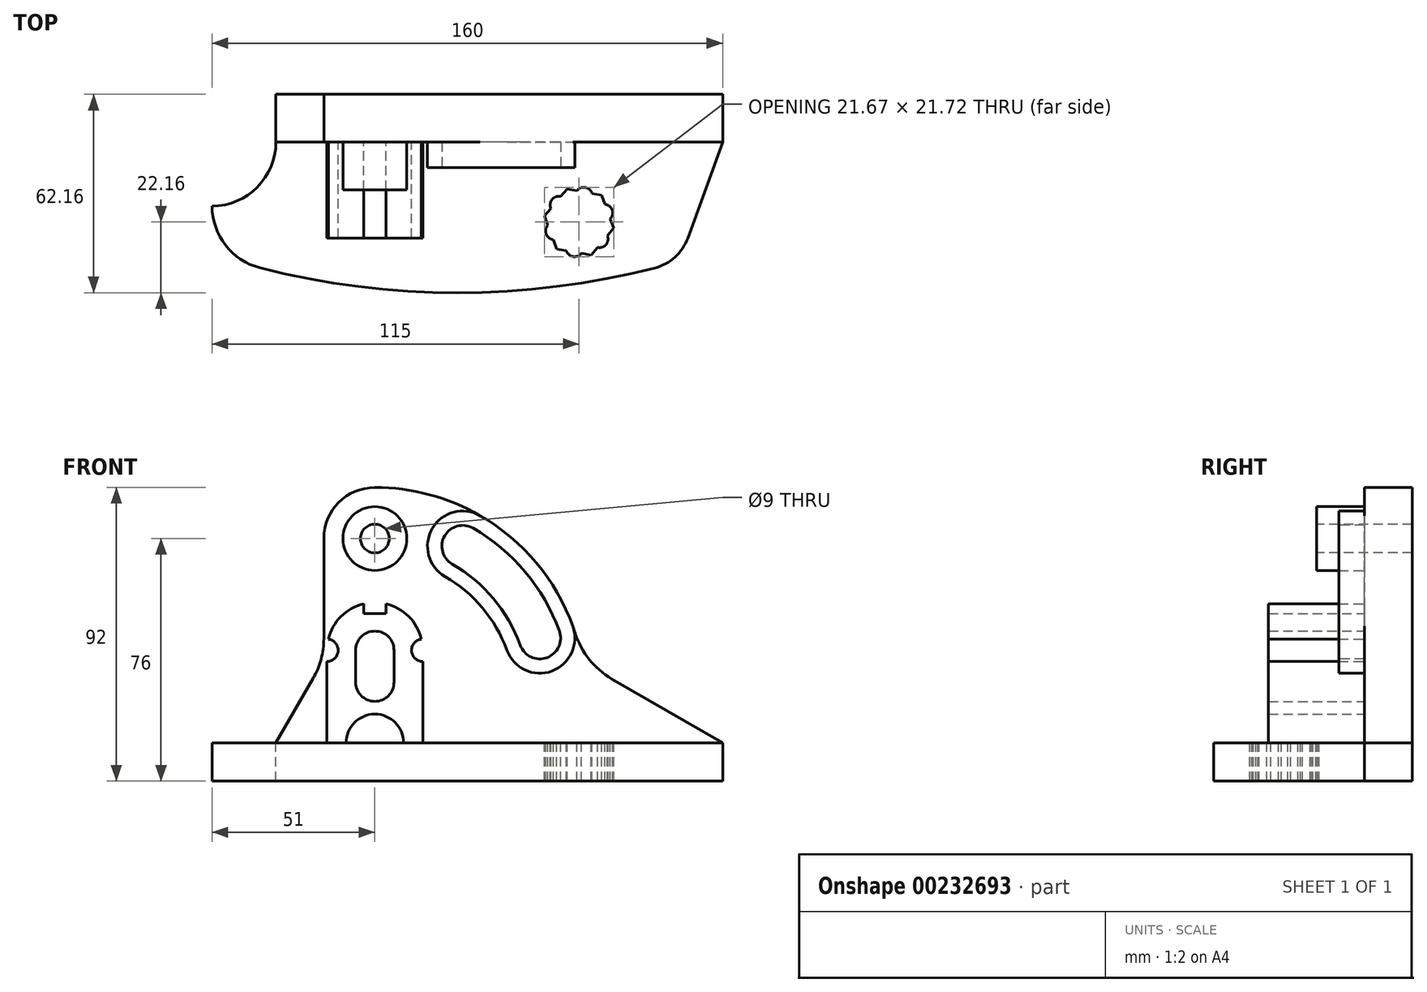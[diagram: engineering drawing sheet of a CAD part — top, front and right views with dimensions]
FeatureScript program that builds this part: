
annotation { "Feature Type Name" : "Feature", "Feature Type Description" : "" }
export const myFeature = defineFeature(function(context is Context, id is Id, definition is map)
    precondition{}
    {
        {
            var Q0;
            Q0=qCreatedBy(makeId("Top.planeOp"),FACE);
            var sketch = newSketch(context, id + "F0", { "sketchPlane" : qUnion([Q0])});
            skLineSegment(sketch, "E0", {"start": v(-31, 15) * mm, "end": v(-31, 0) * mm});
            skLineSegment(sketch, "E1", {"start": v(109, 15) * mm, "end": v(109, 0) * mm});
            skLineSegment(sketch, "E2", {"start": v(-31, 15) * mm, "end": v(109, 15) * mm});
            skLineSegment(sketch, "E3", {"start": v(109, 0) * mm, "end": v(98.08, -30) * mm});
            skArc(sketch, "E4", {"start": v(-51, -20) * mm, "mid": v(-36.86, -14.14) * mm, "end": v(-31, 0) * mm});
            skArc(sketch, "E5", {"start": v(-51, -20) * mm, "mid": v(-46.8, -32.27) * mm, "end": v(-35.95, -39.38) * mm});
            skLineSegment(sketch, "E6.0", {"start": v(94.9, 5.13) * mm, "end": v(83.99, -24.87) * mm, "construction": true});
            skArc(sketch, "E7", {"start": v(87.7, -39.4) * mm, "mid": v(94.05, -36) * mm, "end": v(98.08, -30) * mm});
            skLineSegment(sketch, "E8", {"start": v(98.08, -30) * mm, "end": v(83.99, -24.87) * mm, "construction": true});
            skArc(sketch, "E9", {"start": v(-35.95, -39.38) * mm, "mid": v(25.87, -47.16) * mm, "end": v(87.7, -39.4) * mm});
            skSolve(sketch);
        }
        {
            var Q0;
            Q0 = qSketchRegion(id + "F0", true);
            extrude(context, id + "F1", {"entities" : qUnion([Q0]), "oppositeDirection" : true, "depth" : 12 * mm});
        }
        {
            var Q0;
            Q0=qCreatedBy(makeId("Front.planeOp"),FACE);
            var sketch = newSketch(context, id + "F2", { "sketchPlane" : qUnion([Q0])});
            skLineSegment(sketch, "E10", {"start": v(109, 0) * mm, "end": v(74.16, 20.11) * mm});
            skLineSegment(sketch, "E11", {"start": v(-31, 0) * mm, "end": v(-19.35, 20.18) * mm});
            skLineSegment(sketch, "E12", {"start": v(-16, 65) * mm, "end": v(-16, 32.68) * mm});
            skArc(sketch, "E13.filletArc", {"start": v(-19.35, 20.18) * mm, "mid": v(-16.85, 26.2) * mm, "end": v(-16, 32.68) * mm});
            skArc(sketch, "E14", {"start": v(62.85, 34.14) * mm, "mid": v(38.9, 67.32) * mm, "end": v(0, 80) * mm});
            skArc(sketch, "E15", {"start": v(0, 80) * mm, "mid": v(-11.31, 75.31) * mm, "end": v(-16, 64) * mm});
            skArc(sketch, "E16", {"start": v(62.85, 34.14) * mm, "mid": v(67.2, 26.07) * mm, "end": v(74.16, 20.11) * mm});
            skLineSegment(sketch, "E17", {"start": v(-31, 0) * mm, "end": v(109, 0) * mm});
            skSolve(sketch);
        }
        {
            var Q0;
            Q0 = qSketchRegion(id + "F2", true);
            extrude(context, id + "F3", {"entities" : qUnion([Q0]), "operationType" : NewBodyOperationType.ADD, "oppositeDirection" : true, "depth" : 15 * mm});
        }
        {
            var Q0;
            Q0=makeQuery(id+"F3.opExtrude","CAP_FACE",FACE,{"disambiguationData":[OSD([sQuery(id+"F2.wireOp",EDGE,"E10"),sQuery(id+"F2.wireOp",EDGE,"E11"),sQuery(id+"F2.wireOp",EDGE,"E12"),sQuery(id+"F2.wireOp",EDGE,"E13.filletArc"),sQuery(id+"F2.wireOp",EDGE,"E14"),sQuery(id+"F2.wireOp",EDGE,"E15"),sQuery(id+"F2.wireOp",EDGE,"E16"),sQuery(id+"F2.wireOp",EDGE,"E17")])],"isStart":true});
            var sketch = newSketch(context, id + "F4", { "sketchPlane" : qUnion([Q0])});
            skLineSegment(sketch, "E18", {"start": v(15, 25.5) * mm, "end": v(15, 0) * mm});
            skLineSegment(sketch, "E19.MirrorCS", {"start": v(-15, 25.5) * mm, "end": v(-15, 0) * mm});
            skArc(sketch, "E20", {"start": v(14.6, 32.48) * mm, "mid": v(10.62, 39.6) * mm, "end": v(3.5, 43.59) * mm});
            skPoint(sketch, "E21.orphan", {"position": v(15, 56.83) * mm});
            skPoint(sketch, "E22.orphan", {"position": v(-15, 56.83) * mm});
            skLineSegment(sketch, "E23", {"start": v(-15, 0) * mm, "end": v(-9, 0) * mm});
            skPoint(sketch, "E24.orphan", {"position": v(-15, -26.65) * mm});
            skPoint(sketch, "E25.orphan", {"position": v(15, -26.65) * mm});
            skLineSegment(sketch, "E26", {"start": v(6, 29) * mm, "end": v(6, 19) * mm});
            skLineSegment(sketch, "E27.MirrorCS", {"start": v(-6, 29) * mm, "end": v(-6, 19) * mm});
            skArc(sketch, "E28", {"start": v(-6, 19) * mm, "mid": v(0, 13) * mm, "end": v(6, 19) * mm});
            skArc(sketch, "E29.trimOffspring", {"start": v(6, 29) * mm, "mid": v(0, 35) * mm, "end": v(-6, 29) * mm});
            skPoint(sketch, "E30.orphan", {"position": v(-6, 36.37) * mm});
            skPoint(sketch, "E31.orphan", {"position": v(6, 36.37) * mm});
            skPoint(sketch, "E32.orphan", {"position": v(-6, 6) * mm});
            skPoint(sketch, "E33.orphan", {"position": v(6, 6) * mm});
            skArc(sketch, "E34", {"start": v(9, 0) * mm, "mid": v(0, 9) * mm, "end": v(-9, 0) * mm});
            skLineSegment(sketch, "E35.trimOffspring", {"start": v(9, 0) * mm, "end": v(15, 0) * mm});
            skArc(sketch, "E36", {"start": v(14.6, 32.48) * mm, "mid": v(11.5, 28.8) * mm, "end": v(15, 25.5) * mm});
            skArc(sketch, "E37.MirrorC", {"start": v(-14.6, 32.48) * mm, "mid": v(-11.5, 28.8) * mm, "end": v(-15, 25.5) * mm});
            skLineSegment(sketch, "E38", {"start": v(3.5, 43.59) * mm, "end": v(3.5, 40.5) * mm});
            skLineSegment(sketch, "E39.MirrorCS", {"start": v(-3.5, 43.59) * mm, "end": v(-3.5, 40.5) * mm});
            skLineSegment(sketch, "E40", {"start": v(-3.5, 40.5) * mm, "end": v(3.5, 40.5) * mm});
            skArc(sketch, "E41.trimOffspring", {"start": v(-3.5, 43.59) * mm, "mid": v(-10.62, 39.6) * mm, "end": v(-14.6, 32.48) * mm});
            skPoint(sketch, "E42.orphan", {"position": v(-3.5, 47.7) * mm});
            skPoint(sketch, "E43.orphan", {"position": v(3.5, 47.7) * mm});
            skSolve(sketch);
        }
        {
            var Q0;
            Q0 = qSketchRegion(id + "F4", true);
            extrude(context, id + "F5", {"entities" : qUnion([Q0]), "operationType" : NewBodyOperationType.ADD, "depth" : 30 * mm});
        }
        {
            var Q0;
            {var subQ0=sQuery(id+"F2.wireOp",EDGE,"E12");var subQ1=sQuery(id+"F2.wireOp",EDGE,"E11");var subQ3=sQuery(id+"F2.wireOp",EDGE,"E14");var subQ6=sQuery(id+"F0.wireOp",EDGE,"E0");var subQ7=sQuery(id+"F2.wireOp",EDGE,"E10");var subQ8=sQuery(id+"F2.wireOp",EDGE,"E15");var subQ9=sQuery(id+"F2.wireOp",EDGE,"E13.filletArc");var subQ10=sQuery(id+"F2.wireOp",EDGE,"E16");Q0=makeQuery(id+"F5.boolean.opBoolean","SPLIT",FACE,{"disambiguationData":[TD([makeQuery(id+"F1.opExtrude","SWEPT_FACE",FACE,{"disambiguationData":[OSD([subQ6])]})])],"derivedFrom":makeQuery(id+"F3.opExtrude","CAP_FACE",FACE,{"disambiguationData":[OSD([subQ7,subQ1,subQ0,subQ9,subQ3,subQ8,subQ10,sQuery(id+"F2.wireOp",EDGE,"E17")])],"isStart":true})});}
            var sketch = newSketch(context, id + "F6", { "sketchPlane" : qUnion([Q0])});
            skCircle(sketch, "E44", {"center": v(0, 14) * mm, "radius": 55 * mm, "construction": true});
            skArc(sketch, "E45.0", {"start": v(57.8, 35.03) * mm, "mid": v(47.11, 53.53) * mm, "end": v(30.75, 67.26) * mm, "construction": true});
            skArc(sketch, "E46.0", {"start": v(45.58, 30.59) * mm, "mid": v(37.15, 45.18) * mm, "end": v(24.25, 56) * mm, "construction": true});
            skLineSegment(sketch, "E47", {"start": v(0, 14) * mm, "end": v(66.08, 38.05) * mm, "construction": true});
            skLineSegment(sketch, "E48", {"start": v(0, 14) * mm, "end": v(40.9, 84.85) * mm, "construction": true});
            skArc(sketch, "E49", {"start": v(30.75, 67.26) * mm, "mid": v(21.87, 64.88) * mm, "end": v(24.25, 56) * mm, "construction": true});
            skArc(sketch, "E50", {"start": v(45.58, 30.59) * mm, "mid": v(53.9, 26.7) * mm, "end": v(57.8, 35.03) * mm, "construction": true});
            skArc(sketch, "E51.0", {"start": v(41.35, 29.05) * mm, "mid": v(33.7, 42.28) * mm, "end": v(22, 52.1) * mm});
            skArc(sketch, "E52", {"start": v(33, 71.16) * mm, "mid": v(17.97, 67.13) * mm, "end": v(22, 52.1) * mm});
            skArc(sketch, "E53", {"start": v(41.35, 29.05) * mm, "mid": v(55.45, 22.47) * mm, "end": v(62.02, 36.57) * mm});
            skArc(sketch, "E54", {"start": v(62.02, 36.57) * mm, "mid": v(50.56, 56.42) * mm, "end": v(33, 71.16) * mm});
            skSolve(sketch);
        }
        {
            var Q0;
            Q0 = qSketchRegion(id + "F6", true);
            extrude(context, id + "F7", {"entities" : qUnion([Q0]), "operationType" : NewBodyOperationType.ADD, "depth" : 8 * mm});
        }
        {
            var Q0;
            Q0=makeQuery(id+"F7.opExtrude","CAP_FACE",FACE,{"disambiguationData":[OSD([sQuery(id+"F6.wireOp",EDGE,"E51.0"),sQuery(id+"F6.wireOp",EDGE,"E52"),sQuery(id+"F6.wireOp",EDGE,"E53"),sQuery(id+"F6.wireOp",EDGE,"E54")])],"isStart":false});
            var sketch = newSketch(context, id + "F8", { "sketchPlane" : qUnion([Q0])});
            skArc(sketch, "E55", {"start": v(27.5, 61.63) * mm, "mid": v(42.13, 49.35) * mm, "end": v(51.68, 32.81) * mm, "construction": true});
            skLineSegment(sketch, "E56", {"start": v(0, 14) * mm, "end": v(67.84, 38.7) * mm, "construction": true});
            skArc(sketch, "E57", {"start": v(30.75, 67.26) * mm, "mid": v(21.87, 64.88) * mm, "end": v(24.25, 56) * mm});
            skArc(sketch, "E58", {"start": v(45.58, 30.59) * mm, "mid": v(53.9, 26.7) * mm, "end": v(57.8, 35.03) * mm});
            skArc(sketch, "E59", {"start": v(24.25, 56) * mm, "mid": v(37.15, 45.18) * mm, "end": v(45.58, 30.59) * mm});
            skArc(sketch, "E60", {"start": v(30.75, 67.26) * mm, "mid": v(47.11, 53.53) * mm, "end": v(57.8, 35.03) * mm});
            skSolve(sketch);
        }
        {
            var Q0;
            Q0 = qSketchRegion(id + "F8", true);
            extrude(context, id + "F9", {"entities" : qUnion([Q0]), "operationType" : NewBodyOperationType.REMOVE, "oppositeDirection" : true, "depth" : 8 * mm});
        }
        {
            var Q0;
            {var subQ0=sQuery(id+"F2.wireOp",EDGE,"E12");var subQ1=sQuery(id+"F2.wireOp",EDGE,"E11");var subQ3=sQuery(id+"F2.wireOp",EDGE,"E14");var subQ6=sQuery(id+"F0.wireOp",EDGE,"E0");var subQ7=sQuery(id+"F2.wireOp",EDGE,"E10");var subQ8=sQuery(id+"F2.wireOp",EDGE,"E15");var subQ9=sQuery(id+"F2.wireOp",EDGE,"E13.filletArc");var subQ10=sQuery(id+"F2.wireOp",EDGE,"E16");Q0=makeQuery(id+"F5.boolean.opBoolean","SPLIT",FACE,{"disambiguationData":[TD([makeQuery(id+"F1.opExtrude","SWEPT_FACE",FACE,{"disambiguationData":[OSD([subQ6])]})])],"derivedFrom":makeQuery(id+"F3.opExtrude","CAP_FACE",FACE,{"disambiguationData":[OSD([subQ7,subQ1,subQ0,subQ9,subQ3,subQ8,subQ10,sQuery(id+"F2.wireOp",EDGE,"E17")])],"isStart":true})});}
            var sketch = newSketch(context, id + "F10", { "sketchPlane" : qUnion([Q0])});
            skCircle(sketch, "E61", {"center": v(0, 64) * mm, "radius": 10 * mm});
            skSolve(sketch);
        }
        {
            var Q0;
            Q0 = qSketchRegion(id + "F10", true);
            extrude(context, id + "F11", {"entities" : qUnion([Q0]), "operationType" : NewBodyOperationType.ADD, "depth" : 15 * mm});
        }
        {
            var Q0;
            Q0=makeQuery(id+"F11.opExtrude","CAP_FACE",FACE,{"disambiguationData":[OSD([sQuery(id+"F10.wireOp",EDGE,"E61")])],"isStart":false});
            var sketch = newSketch(context, id + "F12", { "sketchPlane" : qUnion([Q0])});
            skPoint(sketch, "E62", {"position": v(0, 64) * mm});
            skSolve(sketch);
        }
        {
            var Q0;
            Q0=sQuery(id+"F12.wireOp",VERTEX,"E62");
            var Q1;
            Q1=makeQuery(id+"F1.opExtrude","SWEPT_BODY",BODY,{"disambiguationData":[OSD([sQuery(id+"F0.wireOp",EDGE,"E0"),sQuery(id+"F0.wireOp",EDGE,"E1"),sQuery(id+"F0.wireOp",EDGE,"E2"),sQuery(id+"F0.wireOp",EDGE,"E3"),sQuery(id+"F0.wireOp",EDGE,"E4"),sQuery(id+"F0.wireOp",EDGE,"E5"),sQuery(id+"F0.wireOp",EDGE,"E7"),sQuery(id+"F0.wireOp",EDGE,"E9")])]});
            hole(context, id + "F13", {"style" : HoleStyle.SIMPLE, "endStyle" : HoleEndStyle.THROUGH, "holeDiameter" : 9 * mm, "locations" : qUnion([Q0]), "scope" : qUnion([Q1]), "isTappedThrough" : true});
        }
        {
            var Q0;
            Q0=makeQuery(id+"F1.opExtrude","CAP_FACE",FACE,{"disambiguationData":[OSD([sQuery(id+"F0.wireOp",EDGE,"E0"),sQuery(id+"F0.wireOp",EDGE,"E1"),sQuery(id+"F0.wireOp",EDGE,"E2"),sQuery(id+"F0.wireOp",EDGE,"E3"),sQuery(id+"F0.wireOp",EDGE,"E4"),sQuery(id+"F0.wireOp",EDGE,"E5"),sQuery(id+"F0.wireOp",EDGE,"E7"),sQuery(id+"F0.wireOp",EDGE,"E9")])],"isStart":true});
            var sketch = newSketch(context, id + "F14", { "sketchPlane" : qUnion([Q0])});
            skLineSegment(sketch, "E63", {"start": v(75.76, -20.72) * mm, "end": v(-4.4, -49.9) * mm, "construction": true});
            skPoint(sketch, "E64.orphan", {"position": v(64, -25) * mm});
            skLineSegment(sketch, "E65.0", {"start": v(72, -10.38) * mm, "end": v(-8.15, -39.56) * mm, "construction": true});
            skLineSegment(sketch, "E66.0", {"start": v(79.52, -31.06) * mm, "end": v(-0.63, -60.23) * mm, "construction": true});
            skLineSegment(sketch, "E67", {"start": v(64, -25) * mm, "end": v(59.35, -12.22) * mm, "construction": true});
            skLineSegment(sketch, "E68.0", {"start": v(79.56, -35.58) * mm, "end": v(69.69, -8.46) * mm, "construction": true});
            skLineSegment(sketch, "E69.0", {"start": v(58.72, -42.67) * mm, "end": v(49.01, -15.99) * mm, "construction": true});
            skCircle(sketch, "E70.cCircle", {"center": v(64, -25) * mm, "radius": 11 * mm, "construction": true});
            skLineSegment(sketch, "E70.0", {"start": v(60.24, -14.66) * mm, "end": v(63.26, -15.2) * mm});
            skLineSegment(sketch, "E70.1", {"start": v(71.07, -16.57) * mm, "end": v(72.12, -19.45) * mm});
            skLineSegment(sketch, "E70.2", {"start": v(74.83, -26.91) * mm, "end": v(72.86, -29.26) * mm});
            skLineSegment(sketch, "E70.3", {"start": v(67.76, -35.34) * mm, "end": v(64.74, -34.8) * mm});
            skLineSegment(sketch, "E70.4", {"start": v(56.93, -33.43) * mm, "end": v(55.88, -30.55) * mm});
            skLineSegment(sketch, "E70.5", {"start": v(53.17, -23.09) * mm, "end": v(55.14, -20.74) * mm});
            skArc(sketch, "E71", {"start": v(73.78, -24.03) * mm, "mid": v(74.34, -21.24) * mm, "end": v(72.12, -19.45) * mm});
            skArc(sketch, "E72.1.0", {"start": v(68.05, -16.04) * mm, "mid": v(65.91, -14.17) * mm, "end": v(63.26, -15.2) * mm});
            skArc(sketch, "E72.2.0", {"start": v(58.27, -17.01) * mm, "mid": v(55.57, -17.93) * mm, "end": v(55.14, -20.74) * mm});
            skArc(sketch, "E72.3.0", {"start": v(54.22, -25.97) * mm, "mid": v(53.66, -28.76) * mm, "end": v(55.88, -30.55) * mm});
            skArc(sketch, "E72.4.0", {"start": v(59.95, -33.96) * mm, "mid": v(62.09, -35.83) * mm, "end": v(64.74, -34.8) * mm});
            skArc(sketch, "E72.5.0", {"start": v(69.73, -32.99) * mm, "mid": v(72.43, -32.07) * mm, "end": v(72.86, -29.26) * mm});
            skLineSegment(sketch, "E73.trimOffspring", {"start": v(59.95, -33.96) * mm, "end": v(56.93, -33.43) * mm});
            skLineSegment(sketch, "E74.trimOffspring", {"start": v(54.22, -25.97) * mm, "end": v(53.17, -23.09) * mm});
            skLineSegment(sketch, "E75.trimOffspring", {"start": v(58.27, -17.01) * mm, "end": v(60.24, -14.66) * mm});
            skLineSegment(sketch, "E76.trimOffspring", {"start": v(68.05, -16.04) * mm, "end": v(71.07, -16.57) * mm});
            skLineSegment(sketch, "E77.trimOffspring", {"start": v(73.78, -24.03) * mm, "end": v(74.83, -26.91) * mm});
            skLineSegment(sketch, "E78.trimOffspring", {"start": v(69.73, -32.99) * mm, "end": v(67.76, -35.34) * mm});
            skSolve(sketch);
        }
        {
            var Q0;
            Q0 = qSketchRegion(id + "F14", true);
            extrude(context, id + "F15", {"entities" : qUnion([Q0]), "operationType" : NewBodyOperationType.REMOVE, "endBound" : BoundingType.THROUGH_ALL, "oppositeDirection" : true, "depth" : 25 * mm});
        }
    });
